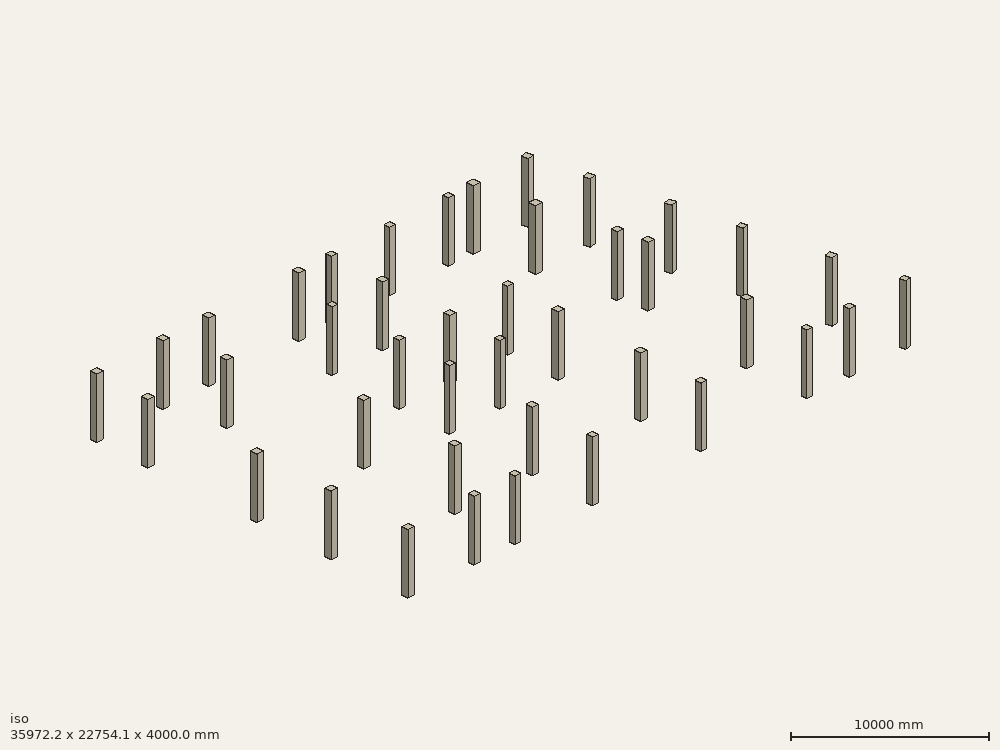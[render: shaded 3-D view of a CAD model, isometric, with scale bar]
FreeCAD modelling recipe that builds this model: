
FCSTD DOCUMENT  (FreeCAD 0.19R24291 (Git))
Label: kazemi
License: All rights reserved
LicenseURL: http://en.wikipedia.org/wiki/All_rights_reserved
objects: Part::FeaturePython×117, App::DocumentObjectGroup×1, App::FeaturePython×1
note: 210 computed .brp shape members not serialized (recipe doc carries the construction recipe); baked Part::Feature solids carry a one-line shape summary decoded from their .brp

FEATURE [Part::FeaturePython] Beam006  # WARN: FeaturePython — macro-defined, semantics opaque (R4)
  end_point = (4740,1600,-2400)
  start_point = (0,1600,-2400)
FEATURE [Part::FeaturePython] Beam007  # WARN: FeaturePython — macro-defined, semantics opaque (R4)
  end_point = (7640,1600,-2400)
  start_point = (4740,1600,-2400)
FEATURE [Part::FeaturePython] Beam008  # WARN: FeaturePython — macro-defined, semantics opaque (R4)
  end_point = (13180,1600,-2400)
  start_point = (7640,1600,-2400)
FEATURE [Part::FeaturePython] Beam009  # WARN: FeaturePython — macro-defined, semantics opaque (R4)
  end_point = (20930,1600,-2400)
  start_point = (13180,1600,-2400)
FEATURE [Part::FeaturePython] Beam010  # WARN: FeaturePython — macro-defined, semantics opaque (R4)
  end_point = (28500,1600,-2400)
  start_point = (20930,1600,-2400)
FEATURE [Part::FeaturePython] Beam011  # WARN: FeaturePython — macro-defined, semantics opaque (R4)
  end_point = (31550,1600,-2400)
  start_point = (28500,1600,-2400)
FEATURE [Part::FeaturePython] Beam012  # WARN: FeaturePython — macro-defined, semantics opaque (R4)
  end_point = (35510,1600,-2400)
  start_point = (31550,1600,-2400)
FEATURE [Part::FeaturePython] Beam013  # WARN: FeaturePython — macro-defined, semantics opaque (R4)
  end_point = (7640,5900,-2400)
  start_point = (7640,1600,-2400)
FEATURE [Part::FeaturePython] Beam014  # WARN: FeaturePython — macro-defined, semantics opaque (R4)
  end_point = (13180,5900,-2400)
  start_point = (13180,1600,-2400)
FEATURE [Part::FeaturePython] Beam015  # WARN: FeaturePython — macro-defined, semantics opaque (R4)
  end_point = (20930,5900,-2400)
  start_point = (20930,1600,-2400)
FEATURE [Part::FeaturePython] Beam016  # WARN: FeaturePython — macro-defined, semantics opaque (R4)
  end_point = (28500,5900,-2400)
  start_point = (28500,1600,-2400)
FEATURE [Part::FeaturePython] Beam017  # WARN: FeaturePython — macro-defined, semantics opaque (R4)
  end_point = (35510,1600,-2400)
  start_point = (34550,5900,-2400)
FEATURE [Part::FeaturePython] Beam018  # WARN: FeaturePython — macro-defined, semantics opaque (R4)
  end_point = (0,7100,-2400)
  start_point = (0,1600,-2400)
FEATURE [Part::FeaturePython] Beam019  # WARN: FeaturePython — macro-defined, semantics opaque (R4)
  end_point = (13180,5900,-2400)
  start_point = (7640,5900,-2400)
FEATURE [Part::FeaturePython] Beam020  # WARN: FeaturePython — macro-defined, semantics opaque (R4)
  end_point = (20930,5900,-2400)
  start_point = (13180,5900,-2400)
FEATURE [Part::FeaturePython] Beam021  # WARN: FeaturePython — macro-defined, semantics opaque (R4)
  end_point = (28500,5900,-2400)
  start_point = (20930,5900,-2400)
FEATURE [Part::FeaturePython] Beam022  # WARN: FeaturePython — macro-defined, semantics opaque (R4)
  end_point = (34550,5900,-2400)
  start_point = (28500,5900,-2400)
FEATURE [Part::FeaturePython] Beam023  # WARN: FeaturePython — macro-defined, semantics opaque (R4)
  end_point = (7640,5900,-2400)
  start_point = (0,7100,-2400)
FEATURE [Part::FeaturePython] Beam024  # WARN: FeaturePython — macro-defined, semantics opaque (R4)
  end_point = (34550,5900,-2400)
  start_point = (33449.5,11180,-2400)
FEATURE [Part::FeaturePython] Beam025  # WARN: FeaturePython — macro-defined, semantics opaque (R4)
  end_point = (13180,11800,-2400)
  start_point = (13180,5900,-2400)
FEATURE [Part::FeaturePython] Beam026  # WARN: FeaturePython — macro-defined, semantics opaque (R4)
  end_point = (20930,11800,-2400)
  start_point = (20930,5900,-2400)
FEATURE [Part::FeaturePython] Beam027  # WARN: FeaturePython — macro-defined, semantics opaque (R4)
  end_point = (7640,12400,-2400)
  start_point = (7640,5900,-2400)
FEATURE [Part::FeaturePython] Beam028  # WARN: FeaturePython — macro-defined, semantics opaque (R4)
  end_point = (29110,13550,-2400)
  start_point = (28500,5900,-2400)
FEATURE [Part::FeaturePython] Beam029  # WARN: FeaturePython — macro-defined, semantics opaque (R4)
  end_point = (0,12400,-2400)
  start_point = (0,7100,-2400)
FEATURE [Part::FeaturePython] Beam030  # WARN: FeaturePython — macro-defined, semantics opaque (R4)
  end_point = (16780,11800,-2400)
  start_point = (13180,11800,-2400)
FEATURE [Part::FeaturePython] Beam031  # WARN: FeaturePython — macro-defined, semantics opaque (R4)
  end_point = (20930,11800,-2400)
  start_point = (16780,11800,-2400)
FEATURE [Part::FeaturePython] Beam032  # WARN: FeaturePython — macro-defined, semantics opaque (R4)
  end_point = (13180,11800,-2400)
  start_point = (7640,12400,-2400)
FEATURE [Part::FeaturePython] Beam033  # WARN: FeaturePython — macro-defined, semantics opaque (R4)
  end_point = (7640,12400,-2400)
  start_point = (0,12400,-2400)
FEATURE [Part::FeaturePython] Beam034  # WARN: FeaturePython — macro-defined, semantics opaque (R4)
  end_point = (29110,13550,-2400)
  start_point = (20930,11800,-2400)
FEATURE [Part::FeaturePython] Beam036  # WARN: FeaturePython — macro-defined, semantics opaque (R4)
  end_point = (33449.5,11180,-2400)
  start_point = (32570,15400,-2400)
FEATURE [Part::FeaturePython] Beam037  # WARN: FeaturePython — macro-defined, semantics opaque (R4)
  end_point = (13180,15400,-2400)
  start_point = (13180,11800,-2400)
FEATURE [Part::FeaturePython] Beam038  # WARN: FeaturePython — macro-defined, semantics opaque (R4)
  end_point = (16780,15400,-2400)
  start_point = (16780,11800,-2400)
FEATURE [Part::FeaturePython] Beam039  # WARN: FeaturePython — macro-defined, semantics opaque (R4)
  end_point = (20930,15400,-2400)
  start_point = (20930,11800,-2400)
FEATURE [Part::FeaturePython] Beam041  # WARN: FeaturePython — macro-defined, semantics opaque (R4)
  end_point = (29110,13550,-2400)
  start_point = (28750,15400,-2400)
FEATURE [Part::FeaturePython] Beam042  # WARN: FeaturePython — macro-defined, semantics opaque (R4)
  end_point = (16780,15400,-2400)
  start_point = (13180,15400,-2400)
FEATURE [Part::FeaturePython] Beam043  # WARN: FeaturePython — macro-defined, semantics opaque (R4)
  end_point = (20930,15400,-2400)
  start_point = (16780,15400,-2400)
FEATURE [Part::FeaturePython] Beam044  # WARN: FeaturePython — macro-defined, semantics opaque (R4)
  end_point = (28750,15400,-2400)
  start_point = (20930,15400,-2400)
FEATURE [Part::FeaturePython] Beam045  # WARN: FeaturePython — macro-defined, semantics opaque (R4)
  end_point = (32570,15400,-2400)
  start_point = (28750,15400,-2400)
FEATURE [Part::FeaturePython] Beam046  # WARN: FeaturePython — macro-defined, semantics opaque (R4)
  end_point = (0,20200,-2400)
  start_point = (0,12400,-2400)
FEATURE [Part::FeaturePython] Beam047  # WARN: FeaturePython — macro-defined, semantics opaque (R4)
  end_point = (7640,12400,-2400)
  start_point = (5640,20200,-2400)
FEATURE [Part::FeaturePython] Beam048  # WARN: FeaturePython — macro-defined, semantics opaque (R4)
  end_point = (13180,20200,-2400)
  start_point = (13180,15400,-2400)
FEATURE [Part::FeaturePython] Beam049  # WARN: FeaturePython — macro-defined, semantics opaque (R4)
  end_point = (16780,20200,-2400)
  start_point = (16780,15400,-2400)
FEATURE [Part::FeaturePython] Beam050  # WARN: FeaturePython — macro-defined, semantics opaque (R4)
  end_point = (28750,15400,-2400)
  start_point = (27720,20200,-2400)
FEATURE [Part::FeaturePython] Beam051  # WARN: FeaturePython — macro-defined, semantics opaque (R4)
  end_point = (32570,15400,-2400)
  start_point = (31550,20200,-2400)
FEATURE [Part::FeaturePython] Beam052  # WARN: FeaturePython — macro-defined, semantics opaque (R4)
  end_point = (5640,20200,-2400)
  start_point = (0,20200,-2400)
FEATURE [Part::FeaturePython] Beam053  # WARN: FeaturePython — macro-defined, semantics opaque (R4)
  end_point = (13180,20200,-2400)
  start_point = (5640,20200,-2400)
FEATURE [Part::FeaturePython] Beam054  # WARN: FeaturePython — macro-defined, semantics opaque (R4)
  end_point = (16780,20200,-2400)
  start_point = (13180,20200,-2400)
FEATURE [Part::FeaturePython] Beam055  # WARN: FeaturePython — macro-defined, semantics opaque (R4)
  end_point = (27720,20200,-2400)
  start_point = (16780,20200,-2400)
FEATURE [Part::FeaturePython] Beam056  # WARN: FeaturePython — macro-defined, semantics opaque (R4)
  end_point = (31550,20200,-2400)
  start_point = (27720,20200,-2400)
FEATURE [Part::FeaturePython] Beam057  # WARN: FeaturePython — macro-defined, semantics opaque (R4)
  end_point = (0,23850,-2400)
  start_point = (0,20200,-2400)
FEATURE [Part::FeaturePython] Beam058  # WARN: FeaturePython — macro-defined, semantics opaque (R4)
  end_point = (5640,20200,-2400)
  start_point = (4740,23850,-2400)
FEATURE [Part::FeaturePython] Beam059  # WARN: FeaturePython — macro-defined, semantics opaque (R4)
  end_point = (16780,23850,-2400)
  start_point = (16780,20200,-2400)
FEATURE [Part::FeaturePython] Beam060  # WARN: FeaturePython — macro-defined, semantics opaque (R4)
  end_point = (31550,20200,-2400)
  start_point = (30780,23850,-2400)
FEATURE [Part::FeaturePython] Beam061  # WARN: FeaturePython — macro-defined, semantics opaque (R4)
  end_point = (4740,23850,-2400)
  start_point = (0,23850,-2400)
FEATURE [Part::FeaturePython] Beam062  # WARN: FeaturePython — macro-defined, semantics opaque (R4)
  end_point = (8000,23850,-2400)
  start_point = (4740,23850,-2400)
FEATURE [Part::FeaturePython] Beam063  # WARN: FeaturePython — macro-defined, semantics opaque (R4)
  end_point = (20930,23850,-2400)
  start_point = (16780,23850,-2400)
FEATURE [Part::FeaturePython] Beam064  # WARN: FeaturePython — macro-defined, semantics opaque (R4)
  end_point = (25130,23850,-2400)
  start_point = (20930,23850,-2400)
FEATURE [Part::FeaturePython] Beam065  # WARN: FeaturePython — macro-defined, semantics opaque (R4)
  end_point = (26950,23850,-2400)
  start_point = (25130,23850,-2400)
FEATURE [Part::FeaturePython] Beam066  # WARN: FeaturePython — macro-defined, semantics opaque (R4)
  end_point = (30780,23850,-2400)
  start_point = (26950,23850,-2400)
FEATURE [Part::FeaturePython] Beam069  # WARN: FeaturePython — macro-defined, semantics opaque (R4)
  end_point = (14430,23850,-2400)
  start_point = (8000,23850,-2400)
FEATURE [Part::FeaturePython] Beam070  # WARN: FeaturePython — macro-defined, semantics opaque (R4)
  end_point = (16780,23850,-2400)
  start_point = (14430,23850,-2400)
FEATURE [Part::FeaturePython] Beam071  # WARN: FeaturePython — macro-defined, semantics opaque (R4)
  end_point = (27720,20200,-2400)
  start_point = (26950,23850,-2400)
FEATURE [Part::FeaturePython] Structure  label="70"  # Arch/BIM 24 (typed FeaturePython)
  FaceMaker = 0
  Height = 4000
  HorizontalArea = 202500
  IfcData = attributes={"GlobalId": {"name": "GlobalId", "type": "IfcGloballyUniqueId", "is_enum": false, "enum_values": []}, "Description": {"... (+438 chars omitted),+1 more (map truncated)
  IfcType = 24
  Length = 450
  MoveBase = false
  MoveWithHost = false
  Nodes = (2) [(-2.22045e-16,-3.03165e-15,0),(-2.22045e-16,-3.03165e-15,4000)]
  NodesOffset = 0
  Normal = (0,0,0)
  PerimeterLength = 1800
  Placement = pos=(0,1600,-2400) rot=(0,0,1;0rad)
  PredefinedType = 0
  VerticalArea = 7.2e+06
  Width = 450
  combos_load = COMB1_Max=204.9869, 19579.89, 23881.76,COMB2_Max=213.6767, 23289.38, 27478.9,COMB3_Max=213.6734, 23294.07, 27476.35,+68 more (map truncated)
FEATURE [Part::FeaturePython] Structure001  label="117"  # Arch/BIM 24 (typed FeaturePython)
  FaceMaker = 0
  Height = 4000
  HorizontalArea = 202500
  IfcData = attributes={"GlobalId": {"name": "GlobalId", "type": "IfcGloballyUniqueId", "is_enum": false, "enum_values": []}, "Description": {"... (+438 chars omitted),+1 more (map truncated)
  IfcType = 24
  Length = 450
  MoveBase = false
  MoveWithHost = false
  Nodes = (2) [(-2.22045e-16,-3.03165e-15,0),(-2.22045e-16,-3.03165e-15,4000)]
  NodesOffset = 0
  Normal = (0,0,0)
  PerimeterLength = 1800
  Placement = pos=(4740,1600,-2400) rot=(0,0,1;0rad)
  PredefinedType = 0
  VerticalArea = 7.2e+06
  Width = 450
  combos_load = COMB1_Max=367.7857, 19514.48, 11342.62,COMB2_Max=400.9117, 25286.11, 12989.73,COMB3_Max=400.7883, 25293.1, 12961.91,+68 more (map truncated)
FEATURE [Part::FeaturePython] Structure002  label="69"  # Arch/BIM 24 (typed FeaturePython)
  FaceMaker = 0
  Height = 4000
  HorizontalArea = 160000
  IfcData = attributes={"GlobalId": {"name": "GlobalId", "type": "IfcGloballyUniqueId", "is_enum": false, "enum_values": []}, "Description": {"... (+438 chars omitted),+1 more (map truncated)
  IfcType = 24
  Length = 400
  MoveBase = false
  MoveWithHost = false
  Nodes = (2) [(-7.77156e-16,0,0),(-7.77156e-16,0,4000)]
  NodesOffset = 0
  Normal = (0,0,0)
  PerimeterLength = 1600
  Placement = pos=(7640,1600,-2400) rot=(0,0,1;0rad)
  PredefinedType = 0
  VerticalArea = 6400000
  Width = 400
  combos_load = COMB1_Max=168.7226, 25616.29, 21300.7,COMB2_Max=176.7744, 29517.62, 21519.84,COMB3_Max=176.8834, 29533.75, 21491.99,+68 more (map truncated)
FEATURE [Part::FeaturePython] Structure003  label="68"  # Arch/BIM 24 (typed FeaturePython)
  FaceMaker = 0
  Height = 4000
  HorizontalArea = 160000
  IfcData = attributes={"GlobalId": {"name": "GlobalId", "type": "IfcGloballyUniqueId", "is_enum": false, "enum_values": []}, "Description": {"... (+438 chars omitted),+1 more (map truncated)
  IfcType = 24
  Length = 400
  MoveBase = false
  MoveWithHost = false
  Nodes = (2) [(-7.77156e-16,0,0),(-7.77156e-16,0,4000)]
  NodesOffset = 0
  Normal = (0,0,0)
  PerimeterLength = 1600
  Placement = pos=(13180,1600,-2400) rot=(0,0,1;0rad)
  PredefinedType = 0
  VerticalArea = 6400000
  Width = 400
  combos_load = COMB1_Max=339.1024, 28076.36, 33832.77,COMB2_Max=389.6557, 32488.12, 39892.66,COMB3_Max=389.6442, 32500.15, 39890.9,+68 more (map truncated)
FEATURE [Part::FeaturePython] Structure004  label="67"  # Arch/BIM 24 (typed FeaturePython)
  FaceMaker = 0
  Height = 4000
  HorizontalArea = 160000
  IfcData = attributes={"GlobalId": {"name": "GlobalId", "type": "IfcGloballyUniqueId", "is_enum": false, "enum_values": []}, "Description": {"... (+438 chars omitted),+1 more (map truncated)
  IfcType = 24
  Length = 400
  MoveBase = false
  MoveWithHost = false
  Nodes = (2) [(-7.77156e-16,0,0),(-7.77156e-16,0,4000)]
  NodesOffset = 0
  Normal = (0,0,0)
  PerimeterLength = 1600
  Placement = pos=(20930,1600,-2400) rot=(0,0,1;0rad)
  PredefinedType = 0
  VerticalArea = 6400000
  Width = 400
  combos_load = COMB1_Max=396.9384, 29012.47, -25663.63,COMB2_Max=453.4432, 33569.27, -32235.64,COMB3_Max=453.4289, 33583.15, -32237.37,+68 more (map truncated)
FEATURE [Part::FeaturePython] Structure005  label="66"  # Arch/BIM 24 (typed FeaturePython)
  FaceMaker = 0
  Height = 4000
  HorizontalArea = 160000
  IfcData = attributes={"GlobalId": {"name": "GlobalId", "type": "IfcGloballyUniqueId", "is_enum": false, "enum_values": []}, "Description": {"... (+438 chars omitted),+1 more (map truncated)
  IfcType = 24
  Length = 400
  MoveBase = false
  MoveWithHost = false
  Nodes = (2) [(-7.77156e-16,0,0),(-7.77156e-16,0,4000)]
  NodesOffset = 0
  Normal = (0,0,0)
  PerimeterLength = 1600
  Placement = pos=(28500,1600,-2400) rot=(0,0,1;0rad)
  PredefinedType = 0
  VerticalArea = 6400000
  Width = 400
  combos_load = COMB1_Max=358.9807, 25870.67, 9168.52,COMB2_Max=395.7822, 29656.58, 16686.87,COMB3_Max=395.6577, 29672.8, 16659.19,+68 more (map truncated)
FEATURE [Part::FeaturePython] Structure006  label="138"  # Arch/BIM 24 (typed FeaturePython)
  FaceMaker = 0
  Height = 4000
  HorizontalArea = 202500
  IfcData = attributes={"GlobalId": {"name": "GlobalId", "type": "IfcGloballyUniqueId", "is_enum": false, "enum_values": []}, "Description": {"... (+438 chars omitted),+1 more (map truncated)
  IfcType = 24
  Length = 450
  MoveBase = false
  MoveWithHost = false
  Nodes = (2) [(-2.22045e-16,-3.03165e-15,0),(-2.22045e-16,-3.03165e-15,4000)]
  NodesOffset = 0
  Normal = (0,0,0)
  PerimeterLength = 1800
  Placement = pos=(31550,1600,-2400) rot=(0,0,1;0rad)
  PredefinedType = 0
  VerticalArea = 7.2e+06
  Width = 450
  combos_load = COMB1_Max=230.39, 18321.26, 23149.42,COMB2_Max=236.3721, 23618.7, 27163.27,COMB3_Max=236.4803, 23624.73, 27134.49,+68 more (map truncated)
FEATURE [Part::FeaturePython] Structure007  label="65"  # Arch/BIM 24 (typed FeaturePython)
  FaceMaker = 0
  Height = 4000
  HorizontalArea = 160000
  IfcData = attributes={"GlobalId": {"name": "GlobalId", "type": "IfcGloballyUniqueId", "is_enum": false, "enum_values": []}, "Description": {"... (+438 chars omitted),+1 more (map truncated)
  IfcType = 24
  Length = 400
  MoveBase = false
  MoveWithHost = false
  Nodes = (2) [(-7.77156e-16,0,0),(-7.77156e-16,0,4000)]
  NodesOffset = 0
  Normal = (0,0,0)
  PerimeterLength = 1600
  Placement = pos=(35510,1600,-2400) rot=(0,0,1;1.78024rad)
  PredefinedType = 0
  VerticalArea = 6400000
  Width = 400
  combos_load = COMB1_Max=164.7017, 17255.78, -6848.21,COMB2_Max=168.6944, 19559.6, -7890.72,COMB3_Max=168.6933, 19561.9, -7891.82,+68 more (map truncated)
FEATURE [Part::FeaturePython] Structure008  label="71"  # Arch/BIM 24 (typed FeaturePython)
  FaceMaker = 0
  Height = 4000
  HorizontalArea = 202500
  IfcData = attributes={"GlobalId": {"name": "GlobalId", "type": "IfcGloballyUniqueId", "is_enum": false, "enum_values": []}, "Description": {"... (+438 chars omitted),+1 more (map truncated)
  IfcType = 24
  Length = 450
  MoveBase = false
  MoveWithHost = false
  Nodes = (2) [(-2.22045e-16,-3.03165e-15,0),(-2.22045e-16,-3.03165e-15,4000)]
  NodesOffset = 0
  Normal = (0,0,0)
  PerimeterLength = 1800
  Placement = pos=(7640,5900,-2400) rot=(0,0,1;0rad)
  PredefinedType = 0
  VerticalArea = 7.2e+06
  Width = 450
  combos_load = COMB1_Max=2455.2133, -23060.86, -9084.66,COMB2_Max=2797.4826, -26624.89, -10542.47,COMB3_Max=2788.6999, -26616.32, -10545.91,+68 more (map truncated)
FEATURE [Part::FeaturePython] Structure009  label="72"  # Arch/BIM 24 (typed FeaturePython)
  FaceMaker = 0
  Height = 4000
  HorizontalArea = 202500
  IfcData = attributes={"GlobalId": {"name": "GlobalId", "type": "IfcGloballyUniqueId", "is_enum": false, "enum_values": []}, "Description": {"... (+438 chars omitted),+1 more (map truncated)
  IfcType = 24
  Length = 450
  MoveBase = false
  MoveWithHost = false
  Nodes = (2) [(-2.22045e-16,-3.03165e-15,0),(-2.22045e-16,-3.03165e-15,4000)]
  NodesOffset = 0
  Normal = (0,0,0)
  PerimeterLength = 1800
  Placement = pos=(13180,5900,-2400) rot=(0,0,1;0rad)
  PredefinedType = 0
  VerticalArea = 7.2e+06
  Width = 450
  combos_load = COMB1_Max=2434.8068, -21823.19, 11899.5,COMB2_Max=2736.8255, -24350.07, 13786.7,COMB3_Max=2728.806, -24343.98, 13785.06,+68 more (map truncated)
FEATURE [Part::FeaturePython] Structure010  label="73"  # Arch/BIM 24 (typed FeaturePython)
  FaceMaker = 0
  Height = 4000
  HorizontalArea = 202500
  IfcData = attributes={"GlobalId": {"name": "GlobalId", "type": "IfcGloballyUniqueId", "is_enum": false, "enum_values": []}, "Description": {"... (+438 chars omitted),+1 more (map truncated)
  IfcType = 24
  Length = 450
  MoveBase = false
  MoveWithHost = false
  Nodes = (2) [(-2.22045e-16,-3.03165e-15,0),(-2.22045e-16,-3.03165e-15,4000)]
  NodesOffset = 0
  Normal = (0,0,0)
  PerimeterLength = 1800
  Placement = pos=(20930,5900,-2400) rot=(0,0,1;0rad)
  PredefinedType = 0
  VerticalArea = 7.2e+06
  Width = 450
  combos_load = COMB1_Max=2847.8465, -16656.99, 5804.87,COMB2_Max=3214.8853, -19219.27, 6276.18,COMB3_Max=3205.1532, -19211.22, 6273.53,+68 more (map truncated)
FEATURE [Part::FeaturePython] Structure011  label="63"  # Arch/BIM 24 (typed FeaturePython)
  FaceMaker = 0
  Height = 4000
  HorizontalArea = 202500
  IfcData = attributes={"GlobalId": {"name": "GlobalId", "type": "IfcGloballyUniqueId", "is_enum": false, "enum_values": []}, "Description": {"... (+438 chars omitted),+1 more (map truncated)
  IfcType = 24
  Length = 450
  MoveBase = false
  MoveWithHost = false
  Nodes = (2) [(-2.22045e-16,-3.03165e-15,0),(-2.22045e-16,-3.03165e-15,4000)]
  NodesOffset = 0
  Normal = (0,0,0)
  PerimeterLength = 1800
  Placement = pos=(28500,5900,-2400) rot=(0,0,1;0rad)
  PredefinedType = 0
  VerticalArea = 7.2e+06
  Width = 450
  combos_load = COMB1_Max=2701.7016, -17054.9, -11857.69,COMB2_Max=3070.2358, -20023.84, -13482.65,COMB3_Max=3060.7579, -20015.95, -13479,+68 more (map truncated)
FEATURE [Part::FeaturePython] Structure012  label="64"  # Arch/BIM 24 (typed FeaturePython)
  FaceMaker = 0
  Height = 4000
  HorizontalArea = 202500
  IfcData = attributes={"GlobalId": {"name": "GlobalId", "type": "IfcGloballyUniqueId", "is_enum": false, "enum_values": []}, "Description": {"... (+438 chars omitted),+1 more (map truncated)
  IfcType = 24
  Length = 450
  MoveBase = false
  MoveWithHost = false
  Nodes = (2) [(-2.22045e-16,-3.03165e-15,0),(-2.22045e-16,-3.03165e-15,4000)]
  NodesOffset = 0
  Normal = (0,0,0)
  PerimeterLength = 1800
  Placement = pos=(34550,5900,-2400) rot=(0,0,1;1.78024rad)
  PredefinedType = 0
  VerticalArea = 7.2e+06
  Width = 450
  combos_load = COMB1_Max=1933.823, -24320.49, -16698.37,COMB2_Max=1901.0639, -28678.75, -19635.69,COMB3_Max=1897.8706, -28667.38, -19630.61,+68 more (map truncated)
FEATURE [Part::FeaturePython] Structure013  label="74"  # Arch/BIM 24 (typed FeaturePython)
  FaceMaker = 0
  Height = 4000
  HorizontalArea = 202500
  IfcData = attributes={"GlobalId": {"name": "GlobalId", "type": "IfcGloballyUniqueId", "is_enum": false, "enum_values": []}, "Description": {"... (+438 chars omitted),+1 more (map truncated)
  IfcType = 24
  Length = 450
  MoveBase = false
  MoveWithHost = false
  Nodes = (2) [(-2.22045e-16,-3.03165e-15,0),(-2.22045e-16,-3.03165e-15,4000)]
  NodesOffset = 0
  Normal = (0,0,0)
  PerimeterLength = 1800
  Placement = pos=(0,7100,-2400) rot=(0,0,1;0rad)
  PredefinedType = 0
  VerticalArea = 7.2e+06
  Width = 450
  combos_load = COMB1_Max=2857.8348, -28141.56, 37594.54,COMB2_Max=2924.0338, -37197.57, 44270.87,COMB3_Max=2917.6777, -37155.36, 44264.23,+68 more (map truncated)
FEATURE [Part::FeaturePython] Structure014  label="136"  # Arch/BIM 24 (typed FeaturePython)
  FaceMaker = 0
  Height = 4000
  HorizontalArea = 160000
  IfcData = attributes={"GlobalId": {"name": "GlobalId", "type": "IfcGloballyUniqueId", "is_enum": false, "enum_values": []}, "Description": {"... (+438 chars omitted),+1 more (map truncated)
  IfcType = 24
  Length = 400
  MoveBase = false
  MoveWithHost = false
  Nodes = (2) [(-7.77156e-16,0,0),(-7.77156e-16,0,4000)]
  NodesOffset = 0
  Normal = (0,0,0)
  PerimeterLength = 1600
  Placement = pos=(33449.5,11180,-2400) rot=(0,0,1;1.78024rad)
  PredefinedType = 0
  VerticalArea = 6400000
  Width = 400
  combos_load = COMB1_Max=1900.746, 4392.18, 995.18,COMB2_Max=1880.6051, 8525.97, 1838.34,COMB3_Max=1877.5536, 8525.67, 1836.92,COMB4_Max=1871.4507, 8525.07, 1834.06,+67 more (map truncated)
FEATURE [Part::FeaturePython] Structure015  label="58"  # Arch/BIM 24 (typed FeaturePython)
  FaceMaker = 0
  Height = 4000
  HorizontalArea = 160000
  IfcData = attributes={"GlobalId": {"name": "GlobalId", "type": "IfcGloballyUniqueId", "is_enum": false, "enum_values": []}, "Description": {"... (+438 chars omitted),+1 more (map truncated)
  IfcType = 24
  Length = 400
  MoveBase = false
  MoveWithHost = false
  Nodes = (2) [(-7.77156e-16,0,0),(-7.77156e-16,0,4000)]
  NodesOffset = 0
  Normal = (0,0,0)
  PerimeterLength = 1600
  Placement = pos=(13180,11800,-2400) rot=(0,0,1;0rad)
  PredefinedType = 0
  VerticalArea = 6400000
  Width = 400
  combos_load = COMB1_Max=2002.2314, 15392.99, -9529.17,COMB2_Max=2119.3246, 17302.35, -11681.08,COMB3_Max=2114.7722, 17303.16, -11685.42,+68 more (map truncated)
FEATURE [Part::FeaturePython] Structure016  label="59"  # Arch/BIM 24 (typed FeaturePython)
  FaceMaker = 0
  Height = 4000
  HorizontalArea = 160000
  IfcData = attributes={"GlobalId": {"name": "GlobalId", "type": "IfcGloballyUniqueId", "is_enum": false, "enum_values": []}, "Description": {"... (+438 chars omitted),+1 more (map truncated)
  IfcType = 24
  Length = 400
  MoveBase = false
  MoveWithHost = false
  Nodes = (2) [(-7.77156e-16,0,0),(-7.77156e-16,0,4000)]
  NodesOffset = 0
  Normal = (0,0,0)
  PerimeterLength = 1600
  Placement = pos=(16780,11800,-2400) rot=(0,0,1;0rad)
  PredefinedType = 0
  VerticalArea = 6400000
  Width = 400
  combos_load = COMB1_Max=1919.2917, -4587.86, 2844.88,COMB2_Max=2019.0352, -5345.83, 3806.61,COMB3_Max=2014.6549, -5343.43, 3794.28,+68 more (map truncated)
FEATURE [Part::FeaturePython] Structure017  label="60"  # Arch/BIM 24 (typed FeaturePython)
  FaceMaker = 0
  Height = 4000
  HorizontalArea = 202500
  IfcData = attributes={"GlobalId": {"name": "GlobalId", "type": "IfcGloballyUniqueId", "is_enum": false, "enum_values": []}, "Description": {"... (+438 chars omitted),+1 more (map truncated)
  IfcType = 24
  Length = 450
  MoveBase = false
  MoveWithHost = false
  Nodes = (2) [(-2.22045e-16,-3.03165e-15,0),(-2.22045e-16,-3.03165e-15,4000)]
  NodesOffset = 0
  Normal = (0,0,0)
  PerimeterLength = 1800
  Placement = pos=(20930,11800,-2400) rot=(0,0,1;0rad)
  PredefinedType = 0
  VerticalArea = 7.2e+06
  Width = 450
  combos_load = COMB1_Max=2423.3979, 2657.5, 36499.11,COMB2_Max=2730.9376, 3016.64, 42950.6,COMB3_Max=2722.6383, 3016.32, 42945.19,+68 more (map truncated)
FEATURE [Part::FeaturePython] Structure018  label="57"  # Arch/BIM 24 (typed FeaturePython)
  FaceMaker = 0
  Height = 4000
  HorizontalArea = 202500
  IfcData = attributes={"GlobalId": {"name": "GlobalId", "type": "IfcGloballyUniqueId", "is_enum": false, "enum_values": []}, "Description": {"... (+438 chars omitted),+1 more (map truncated)
  IfcType = 24
  Length = 450
  MoveBase = false
  MoveWithHost = false
  Nodes = (2) [(-2.22045e-16,-3.03165e-15,0),(-2.22045e-16,-3.03165e-15,4000)]
  NodesOffset = 0
  Normal = (0,0,0)
  PerimeterLength = 1800
  Placement = pos=(0,12400,-2400) rot=(0,0,1;0rad)
  PredefinedType = 0
  VerticalArea = 7.2e+06
  Width = 450
  combos_load = COMB1_Max=2946.6845, 15423.19, 42271.26,COMB2_Max=3019.3212, 23085.13, 49434.52,COMB3_Max=3013.3619, 23125.2, 49428.67,+68 more (map truncated)
FEATURE [Part::FeaturePython] Structure019  label="56"  # Arch/BIM 24 (typed FeaturePython)
  FaceMaker = 0
  Height = 4000
  HorizontalArea = 202500
  IfcData = attributes={"GlobalId": {"name": "GlobalId", "type": "IfcGloballyUniqueId", "is_enum": false, "enum_values": []}, "Description": {"... (+438 chars omitted),+1 more (map truncated)
  IfcType = 24
  Length = 450
  MoveBase = false
  MoveWithHost = false
  Nodes = (2) [(-2.22045e-16,-3.03165e-15,0),(-2.22045e-16,-3.03165e-15,4000)]
  NodesOffset = 0
  Normal = (0,0,0)
  PerimeterLength = 1800
  Placement = pos=(7640,12400,-2400) rot=(0,0,1;0rad)
  PredefinedType = 0
  VerticalArea = 7.2e+06
  Width = 450
  combos_load = COMB1_Max=3180.0042, -6357.13, -23910.33,COMB2_Max=3619.2252, -7306.03, -27332.1,COMB3_Max=3608.0773, -7304.27, -27332.17,+68 more (map truncated)
FEATURE [Part::FeaturePython] Structure020  label="62"  # Arch/BIM 24 (typed FeaturePython)
  FaceMaker = 0
  Height = 4000
  HorizontalArea = 202500
  IfcData = attributes={"GlobalId": {"name": "GlobalId", "type": "IfcGloballyUniqueId", "is_enum": false, "enum_values": []}, "Description": {"... (+438 chars omitted),+1 more (map truncated)
  IfcType = 24
  Length = 450
  MoveBase = false
  MoveWithHost = false
  Nodes = (2) [(-2.22045e-16,-3.03165e-15,0),(-2.22045e-16,-3.03165e-15,4000)]
  NodesOffset = 0
  Normal = (0,0,0)
  PerimeterLength = 1800
  Placement = pos=(29110,13550,-2400) rot=(0,0,1;0rad)
  PredefinedType = 0
  VerticalArea = 7.2e+06
  Width = 450
  combos_load = COMB1_Max=2085.1281, 25546.7, -42164.29,COMB2_Max=2357.6151, 30200.08, -49414.72,COMB3_Max=2350.5314, 30194.44, -49415.47,+68 more (map truncated)
FEATURE [Part::FeaturePython] Structure021  label="55"  # Arch/BIM 24 (typed FeaturePython)
  FaceMaker = 0
  Height = 4000
  HorizontalArea = 160000
  IfcData = attributes={"GlobalId": {"name": "GlobalId", "type": "IfcGloballyUniqueId", "is_enum": false, "enum_values": []}, "Description": {"... (+438 chars omitted),+1 more (map truncated)
  IfcType = 24
  Length = 400
  MoveBase = false
  MoveWithHost = false
  Nodes = (2) [(-7.77156e-16,0,0),(-7.77156e-16,0,4000)]
  NodesOffset = 0
  Normal = (0,0,0)
  PerimeterLength = 1600
  Placement = pos=(13180,15400,-2400) rot=(0,0,1;0rad)
  PredefinedType = 0
  VerticalArea = 6400000
  Width = 400
  combos_load = COMB1_Max=2382.784, -18564.13, 2504.65,COMB2_Max=2549.675, -22507.26, 2701.4,COMB3_Max=2544.2837, -22476.99, 2698.09,+68 more (map truncated)
FEATURE [Part::FeaturePython] Structure022  label="54"  # Arch/BIM 24 (typed FeaturePython)
  FaceMaker = 0
  Height = 4000
  HorizontalArea = 202500
  IfcData = attributes={"GlobalId": {"name": "GlobalId", "type": "IfcGloballyUniqueId", "is_enum": false, "enum_values": []}, "Description": {"... (+438 chars omitted),+1 more (map truncated)
  IfcType = 24
  Length = 450
  MoveBase = false
  MoveWithHost = false
  Nodes = (2) [(-2.22045e-16,-3.03165e-15,0),(-2.22045e-16,-3.03165e-15,4000)]
  NodesOffset = 0
  Normal = (0,0,0)
  PerimeterLength = 1800
  Placement = pos=(16780,15400,-2400) rot=(0,0,1;0rad)
  PredefinedType = 0
  VerticalArea = 7.2e+06
  Width = 450
  combos_load = COMB1_Max=2802.1985, -697.04, 13772.35,COMB2_Max=3055.3966, -1469.11, 16134.33,COMB3_Max=3049.3394, -1448.05, 16126.74,+68 more (map truncated)
FEATURE [Part::FeaturePython] Structure023  label="53"  # Arch/BIM 24 (typed FeaturePython)
  FaceMaker = 0
  Height = 4000
  HorizontalArea = 160000
  IfcData = attributes={"GlobalId": {"name": "GlobalId", "type": "IfcGloballyUniqueId", "is_enum": false, "enum_values": []}, "Description": {"... (+438 chars omitted),+1 more (map truncated)
  IfcType = 24
  Length = 400
  MoveBase = false
  MoveWithHost = false
  Nodes = (2) [(-7.77156e-16,0,0),(-7.77156e-16,0,4000)]
  NodesOffset = 0
  Normal = (0,0,0)
  PerimeterLength = 1600
  Placement = pos=(20930,15400,-2400) rot=(0,0,1;0rad)
  PredefinedType = 0
  VerticalArea = 6400000
  Width = 400
  combos_load = COMB1_Max=1955.8872, 8645.1, 21140.43,COMB2_Max=2150.8582, 10479.18, 23341.89,COMB3_Max=2144.9622, 10479.31, 23338.12,+68 more (map truncated)
FEATURE [Part::FeaturePython] Structure024  label="52"  # Arch/BIM 24 (typed FeaturePython)
  FaceMaker = 0
  Height = 4000
  HorizontalArea = 202500
  IfcData = attributes={"GlobalId": {"name": "GlobalId", "type": "IfcGloballyUniqueId", "is_enum": false, "enum_values": []}, "Description": {"... (+438 chars omitted),+1 more (map truncated)
  IfcType = 24
  Length = 450
  MoveBase = false
  MoveWithHost = false
  Nodes = (2) [(-2.22045e-16,-3.03165e-15,0),(-2.22045e-16,-3.03165e-15,4000)]
  NodesOffset = 0
  Normal = (0,0,0)
  PerimeterLength = 1800
  Placement = pos=(28750,15400,-2400) rot=(0,0,1;0rad)
  PredefinedType = 0
  VerticalArea = 7.2e+06
  Width = 450
  combos_load = COMB1_Max=1727.1101, 961.69, -16873.92,COMB2_Max=1885.8713, 1802, -18814.09,COMB3_Max=1880.7547, 1803.51, -18805.73,+68 more (map truncated)
FEATURE [Part::FeaturePython] Structure025  label="51"  # Arch/BIM 24 (typed FeaturePython)
  FaceMaker = 0
  Height = 4000
  HorizontalArea = 202500
  IfcData = attributes={"GlobalId": {"name": "GlobalId", "type": "IfcGloballyUniqueId", "is_enum": false, "enum_values": []}, "Description": {"... (+438 chars omitted),+1 more (map truncated)
  IfcType = 24
  Length = 450
  MoveBase = false
  MoveWithHost = false
  Nodes = (2) [(-2.22045e-16,-3.03165e-15,0),(-2.22045e-16,-3.03165e-15,4000)]
  NodesOffset = 0
  Normal = (0,0,0)
  PerimeterLength = 1800
  Placement = pos=(32570,15400,-2400) rot=(0,0,1;1.78024rad)
  PredefinedType = 0
  VerticalArea = 7.2e+06
  Width = 450
  combos_load = COMB1_Max=936.8762, 1780.49, -294.99,COMB2_Max=947.3289, 2748.35, -255.13,COMB3_Max=945.6114, 2749.57, -246.43,COMB4_Max=942.1764, 2752, -229.04,+67 more (map truncated)
FEATURE [Part::FeaturePython] Structure026  label="45"  # Arch/BIM 24 (typed FeaturePython)
  FaceMaker = 0
  Height = 4000
  HorizontalArea = 202500
  IfcData = attributes={"GlobalId": {"name": "GlobalId", "type": "IfcGloballyUniqueId", "is_enum": false, "enum_values": []}, "Description": {"... (+438 chars omitted),+1 more (map truncated)
  IfcType = 24
  Length = 450
  MoveBase = false
  MoveWithHost = false
  Nodes = (2) [(-2.22045e-16,-3.03165e-15,0),(-2.22045e-16,-3.03165e-15,4000)]
  NodesOffset = 0
  Normal = (0,0,0)
  PerimeterLength = 1800
  Placement = pos=(0,20200,-2400) rot=(0,0,1;0rad)
  PredefinedType = 0
  VerticalArea = 7.2e+06
  Width = 450
  combos_load = COMB1_Max=1580.4876, 6176.86, 19719.26,COMB2_Max=1660.7851, 4146.38, 23037.39,COMB3_Max=1657.0031, 4146.82, 23033.89,+68 more (map truncated)
FEATURE [Part::FeaturePython] Structure027  label="46"  # Arch/BIM 24 (typed FeaturePython)
  FaceMaker = 0
  Height = 4000
  HorizontalArea = 202500
  IfcData = attributes={"GlobalId": {"name": "GlobalId", "type": "IfcGloballyUniqueId", "is_enum": false, "enum_values": []}, "Description": {"... (+438 chars omitted),+1 more (map truncated)
  IfcType = 24
  Length = 450
  MoveBase = false
  MoveWithHost = false
  Nodes = (2) [(-2.22045e-16,-3.03165e-15,0),(-2.22045e-16,-3.03165e-15,4000)]
  NodesOffset = 0
  Normal = (0,0,0)
  PerimeterLength = 1800
  Placement = pos=(5640,20200,-2400) rot=(0,0,1;0rad)
  PredefinedType = 0
  VerticalArea = 7.2e+06
  Width = 450
  combos_load = COMB1_Max=2717.9805, 29858.55, 4301.37,COMB2_Max=3083.3201, 34803.25, 5057.83,COMB3_Max=3073.8958, 34799.3, 5054.62,+68 more (map truncated)
FEATURE [Part::FeaturePython] Structure028  label="47"  # Arch/BIM 24 (typed FeaturePython)
  FaceMaker = 0
  Height = 4000
  HorizontalArea = 160000
  IfcData = attributes={"GlobalId": {"name": "GlobalId", "type": "IfcGloballyUniqueId", "is_enum": false, "enum_values": []}, "Description": {"... (+438 chars omitted),+1 more (map truncated)
  IfcType = 24
  Length = 400
  MoveBase = false
  MoveWithHost = false
  Nodes = (2) [(-7.77156e-16,0,0),(-7.77156e-16,0,4000)]
  NodesOffset = 0
  Normal = (0,0,0)
  PerimeterLength = 1600
  Placement = pos=(13180,20200,-2400) rot=(0,0,1;0rad)
  PredefinedType = 0
  VerticalArea = 6400000
  Width = 400
  combos_load = COMB1_Max=2384.2914, 22153.18, -8879.16,COMB2_Max=2551.0793, 27811.63, -10566.94,COMB3_Max=2545.9626, 27828.96, -10568.9,+68 more (map truncated)
FEATURE [Part::FeaturePython] Structure029  label="48"  # Arch/BIM 24 (typed FeaturePython)
  FaceMaker = 0
  Height = 4000
  HorizontalArea = 202500
  IfcData = attributes={"GlobalId": {"name": "GlobalId", "type": "IfcGloballyUniqueId", "is_enum": false, "enum_values": []}, "Description": {"... (+438 chars omitted),+1 more (map truncated)
  IfcType = 24
  Length = 450
  MoveBase = false
  MoveWithHost = false
  Nodes = (2) [(-2.22045e-16,-3.03165e-15,0),(-2.22045e-16,-3.03165e-15,4000)]
  NodesOffset = 0
  Normal = (0,0,0)
  PerimeterLength = 1800
  Placement = pos=(16780,20200,-2400) rot=(0,0,1;0rad)
  PredefinedType = 0
  VerticalArea = 7.2e+06
  Width = 450
  combos_load = COMB1_Max=2795.4973, -11645.67, 58872.24,COMB2_Max=3055.0798, -14908.92, 67577.38,COMB3_Max=3049.2803, -14888.82, 67570.21,+68 more (map truncated)
FEATURE [Part::FeaturePython] Structure030  label="49"  # Arch/BIM 24 (typed FeaturePython)
  FaceMaker = 0
  Height = 4000
  HorizontalArea = 250000
  IfcData = attributes={"GlobalId": {"name": "GlobalId", "type": "IfcGloballyUniqueId", "is_enum": false, "enum_values": []}, "Description": {"... (+438 chars omitted),+1 more (map truncated)
  IfcType = 24
  Length = 500
  MoveBase = false
  MoveWithHost = false
  Nodes = (2) [(-2.10942e-15,-7.27596e-15,0),(-2.10942e-15,-7.27596e-15,4000)]
  NodesOffset = 0
  Normal = (0,0,0)
  PerimeterLength = 2000
  Placement = pos=(27720,20200,-2400) rot=(0,0,1;0rad)
  PredefinedType = 0
  VerticalArea = 8e+06
  Width = 500
  combos_load = COMB1_Max=2232.2185, 6597.48, -46279.97,COMB2_Max=2499.1371, 8124.71, -56087.4,COMB3_Max=2491.9007, 8106.31, -56087.48,+68 more (map truncated)
FEATURE [Part::FeaturePython] Structure031  label="50"  # Arch/BIM 24 (typed FeaturePython)
  FaceMaker = 0
  Height = 4000
  HorizontalArea = 202500
  IfcData = attributes={"GlobalId": {"name": "GlobalId", "type": "IfcGloballyUniqueId", "is_enum": false, "enum_values": []}, "Description": {"... (+438 chars omitted),+1 more (map truncated)
  IfcType = 24
  Length = 450
  MoveBase = false
  MoveWithHost = false
  Nodes = (2) [(-2.22045e-16,-3.03165e-15,0),(-2.22045e-16,-3.03165e-15,4000)]
  NodesOffset = 0
  Normal = (0,0,0)
  PerimeterLength = 1800
  Placement = pos=(31550,20200,-2400) rot=(0,0,1;1.78024rad)
  PredefinedType = 0
  VerticalArea = 7.2e+06
  Width = 450
  combos_load = COMB1_Max=1052.8168, -955.08, -6865.03,COMB2_Max=1097.8069, -976.88, -7312.06,COMB3_Max=1095.2905, -977.32, -7308.95,+68 more (map truncated)
FEATURE [Part::FeaturePython] Structure032  label="32"  # Arch/BIM 24 (typed FeaturePython)
  FaceMaker = 0
  Height = 4000
  HorizontalArea = 202500
  IfcData = attributes={"GlobalId": {"name": "GlobalId", "type": "IfcGloballyUniqueId", "is_enum": false, "enum_values": []}, "Description": {"... (+438 chars omitted),+1 more (map truncated)
  IfcType = 24
  Length = 450
  MoveBase = false
  MoveWithHost = false
  Nodes = (2) [(-2.22045e-16,-3.03165e-15,0),(-2.22045e-16,-3.03165e-15,4000)]
  NodesOffset = 0
  Normal = (0,0,0)
  PerimeterLength = 1800
  Placement = pos=(0,23850,-2400) rot=(0,0,1;0rad)
  PredefinedType = 0
  VerticalArea = 7.2e+06
  Width = 450
  combos_load = COMB1_Max=810.6912, 7574.91, 5394.06,COMB2_Max=843.1205, 8450.9, 5263.39,COMB3_Max=841.1557, 8450.96, 5261.37,COMB4_Max=837.2263, 8451.1, 5257.34,+67 more (map truncated)
FEATURE [Part::FeaturePython] Structure033  label="39"  # Arch/BIM 24 (typed FeaturePython)
  FaceMaker = 0
  Height = 4000
  HorizontalArea = 202500
  IfcData = attributes={"GlobalId": {"name": "GlobalId", "type": "IfcGloballyUniqueId", "is_enum": false, "enum_values": []}, "Description": {"... (+438 chars omitted),+1 more (map truncated)
  IfcType = 24
  Length = 450
  MoveBase = false
  MoveWithHost = false
  Nodes = (2) [(-2.22045e-16,-3.03165e-15,0),(-2.22045e-16,-3.03165e-15,4000)]
  NodesOffset = 0
  Normal = (0,0,0)
  PerimeterLength = 1800
  Placement = pos=(4740,23850,-2400) rot=(0,0,1;0rad)
  PredefinedType = 0
  VerticalArea = 7.2e+06
  Width = 450
  combos_load = COMB1_Max=1662.7741, 6908.71, 5342.49,COMB2_Max=1717.1628, 8035.47, 8254.92,COMB3_Max=1713.328, 8033.4, 8239.92,COMB4_Max=1705.6584, 8029.28, 8209.91,+67 more (map truncated)
FEATURE [Part::FeaturePython] Structure034  label="40"  # Arch/BIM 24 (typed FeaturePython)
  FaceMaker = 0
  Height = 4000
  HorizontalArea = 202500
  IfcData = attributes={"GlobalId": {"name": "GlobalId", "type": "IfcGloballyUniqueId", "is_enum": false, "enum_values": []}, "Description": {"... (+438 chars omitted),+1 more (map truncated)
  IfcType = 24
  Length = 450
  MoveBase = false
  MoveWithHost = false
  Nodes = (2) [(-2.22045e-16,-3.03165e-15,0),(-2.22045e-16,-3.03165e-15,4000)]
  NodesOffset = 0
  Normal = (0,0,0)
  PerimeterLength = 1800
  Placement = pos=(8000,23850,-2400) rot=(0,0,1;0rad)
  PredefinedType = 0
  VerticalArea = 7.2e+06
  Width = 450
  combos_load = COMB1_Max=1581.3367, 3238.01, 14097.08,COMB2_Max=1614.81, 3621.96, 15988.22,COMB3_Max=1611.1537, 3624.16, 15975.32,+68 more (map truncated)
FEATURE [Part::FeaturePython] Structure035  label="41"  # Arch/BIM 24 (typed FeaturePython)
  FaceMaker = 0
  Height = 4000
  HorizontalArea = 160000
  IfcData = attributes={"GlobalId": {"name": "GlobalId", "type": "IfcGloballyUniqueId", "is_enum": false, "enum_values": []}, "Description": {"... (+438 chars omitted),+1 more (map truncated)
  IfcType = 24
  Length = 400
  MoveBase = false
  MoveWithHost = false
  Nodes = (2) [(-7.77156e-16,0,0),(-7.77156e-16,0,4000)]
  NodesOffset = 0
  Normal = (0,0,0)
  PerimeterLength = 1600
  Placement = pos=(16780,23850,-2400) rot=(0,0,1;0rad)
  PredefinedType = 0
  VerticalArea = 6400000
  Width = 400
  combos_load = COMB1_Max=1892.5081, 6952.88, -2653.5,COMB2_Max=1954.7064, 8612.64, -1483.05,COMB3_Max=1950.5111, 8615.09, -1513.5,+68 more (map truncated)
FEATURE [Part::FeaturePython] Structure036  label="164"  # Arch/BIM 24 (typed FeaturePython)
  FaceMaker = 0
  Height = 4000
  HorizontalArea = 160000
  IfcData = attributes={"GlobalId": {"name": "GlobalId", "type": "IfcGloballyUniqueId", "is_enum": false, "enum_values": []}, "Description": {"... (+438 chars omitted),+1 more (map truncated)
  IfcType = 24
  Length = 400
  MoveBase = false
  MoveWithHost = false
  Nodes = (2) [(-7.77156e-16,0,0),(-7.77156e-16,0,4000)]
  NodesOffset = 0
  Normal = (0,0,0)
  PerimeterLength = 1600
  Placement = pos=(20930,23850,-2400) rot=(0,0,1;0rad)
  PredefinedType = 0
  VerticalArea = 6400000
  Width = 400
  combos_load = COMB1_Max=1756.8905, 1851.96, 11182.67,COMB2_Max=1785.5084, 2131.63, 13054.5,COMB3_Max=1781.5911, 2133.54, 13028.17,+68 more (map truncated)
FEATURE [Part::FeaturePython] Structure037  label="43"  # Arch/BIM 24 (typed FeaturePython)
  FaceMaker = 0
  Height = 4000
  HorizontalArea = 160000
  IfcData = attributes={"GlobalId": {"name": "GlobalId", "type": "IfcGloballyUniqueId", "is_enum": false, "enum_values": []}, "Description": {"... (+438 chars omitted),+1 more (map truncated)
  IfcType = 24
  Length = 400
  MoveBase = false
  MoveWithHost = false
  Nodes = (2) [(-7.77156e-16,0,0),(-7.77156e-16,0,4000)]
  NodesOffset = 0
  Normal = (0,0,0)
  PerimeterLength = 1600
  Placement = pos=(25130,23850,-2400) rot=(0,0,1;0rad)
  PredefinedType = 0
  VerticalArea = 6400000
  Width = 400
  combos_load = COMB1_Max=1165.8927, -99.26, -7899.42,COMB2_Max=1280.0021, -287.83, -8439.13,COMB3_Max=1275.995, -288.22, -8426.94,+68 more (map truncated)
FEATURE [Part::FeaturePython] Structure038  label="131"  # Arch/BIM 24 (typed FeaturePython)
  FaceMaker = 0
  Height = 4000
  HorizontalArea = 250000
  IfcData = attributes={"GlobalId": {"name": "GlobalId", "type": "IfcGloballyUniqueId", "is_enum": false, "enum_values": []}, "Description": {"... (+438 chars omitted),+1 more (map truncated)
  IfcType = 24
  Length = 500
  MoveBase = false
  MoveWithHost = false
  Nodes = (2) [(-2.10942e-15,-7.27596e-15,0),(-2.10942e-15,-7.27596e-15,4000)]
  NodesOffset = 0
  Normal = (0,0,0)
  PerimeterLength = 2000
  Placement = pos=(26950,23850,-2400) rot=(0,0,1;0rad)
  PredefinedType = 0
  VerticalArea = 8e+06
  Width = 500
  combos_load = COMB1_Max=184.9319, 23760.84, 11032.13,COMB2_Max=187.4071, 26127.84, 10805.72,COMB3_Max=187.239, 26081.07, 10817.96,+68 more (map truncated)
FEATURE [Part::FeaturePython] Structure039  label="115"  # Arch/BIM 24 (typed FeaturePython)
  FaceMaker = 0
  Height = 4000
  HorizontalArea = 202500
  IfcData = attributes={"GlobalId": {"name": "GlobalId", "type": "IfcGloballyUniqueId", "is_enum": false, "enum_values": []}, "Description": {"... (+438 chars omitted),+1 more (map truncated)
  IfcType = 24
  Length = 450
  MoveBase = false
  MoveWithHost = false
  Nodes = (2) [(-2.22045e-16,-3.03165e-15,0),(-2.22045e-16,-3.03165e-15,4000)]
  NodesOffset = 0
  Normal = (0,0,0)
  PerimeterLength = 1800
  Placement = pos=(30780,23850,-2400) rot=(0,0,1;1.78024rad)
  PredefinedType = 0
  VerticalArea = 7.2e+06
  Width = 450
  combos_load = COMB1_Max=620.3994, 8424.26, -4478.92,COMB2_Max=639.5038, 8174.31, -4233.64,COMB3_Max=638.164, 8172.5, -4238.45,COMB4_Max=635.4843, 8168.87, -4248.06,+67 more (map truncated)
FEATURE [Part::FeaturePython] Structure040  label="299"  # Arch/BIM 24 (typed FeaturePython)
  FaceMaker = 0
  Height = 4000
  HorizontalArea = 202500
  IfcData = attributes={"GlobalId": {"name": "GlobalId", "type": "IfcGloballyUniqueId", "is_enum": false, "enum_values": []}, "Description": {"... (+438 chars omitted),+1 more (map truncated)
  IfcType = 24
  Length = 450
  MoveBase = false
  MoveWithHost = false
  Nodes = (2) [(-2.22045e-16,-3.03165e-15,0),(-2.22045e-16,-3.03165e-15,4000)]
  NodesOffset = 0
  Normal = (0,0,0)
  PerimeterLength = 1800
  Placement = pos=(14430,23850,-2400) rot=(0,0,1;0rad)
  PredefinedType = 0
  VerticalArea = 7.2e+06
  Width = 450
  combos_load = COMB1_Max=170.8135, 12716.05, 5086.31,COMB2_Max=196.6652, 15705.83, 6474.11,COMB3_Max=196.639, 15704.74, 6467.55,+68 more (map truncated)
FEATURE [App::DocumentObjectGroup] Columns
  Group = -> [Structure,Structure001,Structure002,Structure003,Structure004,Structure005,Structure006,Structure007,Structure008,Structure009,Structure010,Structure011,Structure012,Structure013,Structure014,Structure015,Structure016,Structure017,Structure018,Structure019,Structure020,Structure021,Structure022,Structure023,Structure024,Structure025,Structure026,Structure027,Structure028,Structure029,Structure030,+10 more]
FEATURE [App::FeaturePython] Safe  # WARN: FeaturePython — macro-defined, semantics opaque (R4)
  input = <path> Model 100%.F2k
  output = <path> Model 100%_export.F2k
FEATURE [Part::FeaturePython] BaseFoundation  # WARN: FeaturePython — macro-defined, semantics opaque (R4)
  Ks = 1.5
  beams = -> [Beam006,Beam007,Beam008,Beam009,Beam010,Beam011,Beam012]
  design_type = 0
  final_wire_first_point = (0,0,0)
  final_wire_last_point = (0,0,0)
  fix_width_from = 2
  height = 1200
  layer = 0
  left_width = 500
  main_wire_first_point = (0,1600,-2400)
  main_wire_last_point = (35510,1600,-2400)
  right_width = 250
  width = 2000
FEATURE [Part::FeaturePython] BaseFoundation001  # WARN: FeaturePython — macro-defined, semantics opaque (R4)
  Ks = 1.5
  beams = -> [Beam018,Beam029,Beam046,Beam057]
  design_type = 0
  final_wire_first_point = (0,0,0)
  final_wire_last_point = (0,0,0)
  fix_width_from = 1
  height = 1200
  layer = 1
  left_width = 300
  main_wire_first_point = (0,1600,-2400)
  main_wire_last_point = (0,23850,-2400)
  right_width = 300
  width = 2000
FEATURE [Part::FeaturePython] BaseFoundation002  # WARN: FeaturePython — macro-defined, semantics opaque (R4)
  Ks = 2
  beams = -> [Beam023,Beam019,Beam020,Beam021,Beam022]
  design_type = 0
  final_wire_first_point = (0,0,0)
  final_wire_last_point = (0,0,0)
  fix_width_from = 0
  height = 1000
  layer = 0
  left_width = 500
  main_wire_first_point = (0,7100,-2400)
  main_wire_last_point = (34550,5900,-2400)
  right_width = 500
  width = 1000
FEATURE [Part::FeaturePython] BaseFoundation003  # WARN: FeaturePython — macro-defined, semantics opaque (R4)
  Ks = 2
  beams = -> [Beam033,Beam032,Beam030,Beam031,Beam034]
  design_type = 0
  final_wire_first_point = (0,0,0)
  final_wire_last_point = (0,0,0)
  fix_width_from = 0
  height = 1000
  layer = 0
  left_width = 500
  main_wire_first_point = (0,12400,-2400)
  main_wire_last_point = (29110,13550,-2400)
  right_width = 500
  width = 1000
FEATURE [Part::FeaturePython] BaseFoundation004  # WARN: FeaturePython — macro-defined, semantics opaque (R4)
  Ks = 2
  beams = -> [Beam052,Beam053,Beam054,Beam055,Beam056]
  design_type = 0
  final_wire_first_point = (0,0,0)
  final_wire_last_point = (0,0,0)
  fix_width_from = 0
  height = 1000
  layer = 0
  left_width = 500
  main_wire_first_point = (0,20200,-2400)
  main_wire_last_point = (31550,20200,-2400)
  right_width = 500
  width = 1000
FEATURE [Part::FeaturePython] BaseFoundation005  # WARN: FeaturePython — macro-defined, semantics opaque (R4)
  Ks = 1.5
  beams = -> [Beam061,Beam062,Beam069,Beam070,Beam063,Beam064,Beam065,Beam066]
  design_type = 0
  final_wire_first_point = (0,0,0)
  final_wire_last_point = (0,0,0)
  fix_width_from = 1
  height = 1000
  layer = 0
  left_width = 300
  main_wire_first_point = (0,23850,-2400)
  main_wire_last_point = (30780,23850,-2400)
  right_width = 500
  width = 1500
FEATURE [Part::FeaturePython] BaseFoundation006  # WARN: FeaturePython — macro-defined, semantics opaque (R4)
  Ks = 2
  beams = -> [Beam058,Beam047,Beam027,Beam013]
  design_type = 0
  final_wire_first_point = (0,0,0)
  final_wire_last_point = (0,0,0)
  fix_width_from = 0
  height = 1000
  layer = 1
  left_width = 500
  main_wire_first_point = (4740,23850,-2400)
  main_wire_last_point = (7640,1600,-2400)
  right_width = 500
  width = 1000
FEATURE [Part::FeaturePython] BaseFoundation007  # WARN: FeaturePython — macro-defined, semantics opaque (R4)
  Ks = 2
  beams = -> [Beam014,Beam025,Beam037,Beam048]
  design_type = 0
  final_wire_first_point = (0,0,0)
  final_wire_last_point = (0,0,0)
  fix_width_from = 0
  height = 1000
  layer = 1
  left_width = 500
  main_wire_first_point = (13180,1600,-2400)
  main_wire_last_point = (13180,20200,-2400)
  right_width = 500
  width = 1000
FEATURE [Part::FeaturePython] BaseFoundation008  # WARN: FeaturePython — macro-defined, semantics opaque (R4)
  Ks = 2
  beams = -> [Beam042,Beam043,Beam044,Beam045]
  design_type = 0
  final_wire_first_point = (0,0,0)
  final_wire_last_point = (0,0,0)
  fix_width_from = 0
  height = 1000
  layer = 0
  left_width = 500
  main_wire_first_point = (13180,15400,-2400)
  main_wire_last_point = (32570,15400,-2400)
  right_width = 500
  width = 1000
FEATURE [Part::FeaturePython] BaseFoundation009  # WARN: FeaturePython — macro-defined, semantics opaque (R4)
  Ks = 2
  beams = -> [Beam038,Beam049,Beam059]
  design_type = 0
  final_wire_first_point = (0,0,0)
  final_wire_last_point = (0,0,0)
  fix_width_from = 0
  height = 1000
  layer = 1
  left_width = 500
  main_wire_first_point = (16780,11800,-2400)
  main_wire_last_point = (16780,23850,-2400)
  right_width = 500
  width = 1000
FEATURE [Part::FeaturePython] BaseFoundation010  # WARN: FeaturePython — macro-defined, semantics opaque (R4)
  Ks = 2
  beams = -> [Beam015,Beam026,Beam039]
  design_type = 0
  final_wire_first_point = (0,0,0)
  final_wire_last_point = (0,0,0)
  fix_width_from = 0
  height = 1000
  layer = 1
  left_width = 500
  main_wire_first_point = (20930,1600,-2400)
  main_wire_last_point = (20930,15400,-2400)
  right_width = 500
  width = 1000
FEATURE [Part::FeaturePython] BaseFoundation011  # WARN: FeaturePython — macro-defined, semantics opaque (R4)
  Ks = 2
  beams = -> [Beam071,Beam050,Beam041,Beam028,Beam016]
  design_type = 0
  final_wire_first_point = (0,0,0)
  final_wire_last_point = (0,0,0)
  fix_width_from = 0
  height = 1000
  layer = 1
  left_width = 500
  main_wire_first_point = (26950,23850,-2400)
  main_wire_last_point = (28500,1600,-2400)
  right_width = 500
  width = 1000
FEATURE [Part::FeaturePython] BaseFoundation012  # WARN: FeaturePython — macro-defined, semantics opaque (R4)
  Ks = 1.5
  beams = -> [Beam060,Beam051,Beam036,Beam024,Beam017]
  design_type = 0
  final_wire_first_point = (0,0,0)
  final_wire_last_point = (0,0,0)
  fix_width_from = 1
  height = 1200
  layer = 1
  left_width = 300
  main_wire_first_point = (30780,23850,-2400)
  main_wire_last_point = (35510,1600,-2400)
  right_width = 300
  width = 2000
FEATURE [Part::FeaturePython] Foundation  # WARN: FeaturePython — macro-defined, semantics opaque (R4)
  base_foundations = -> [BaseFoundation,BaseFoundation001,BaseFoundation002,BaseFoundation003,BaseFoundation004,BaseFoundation005,BaseFoundation006,BaseFoundation007,BaseFoundation008,BaseFoundation009,BaseFoundation010,BaseFoundation011,BaseFoundation012]
  continuous_layer = 0
  cover = 75
  d = 0
  fc = 25000
  foundation_type = 0
  height = 0
  level = -2400
  redraw = false
note: 2 file-system paths scrubbed to <path> (originals preserved in the JSON sidecar)
